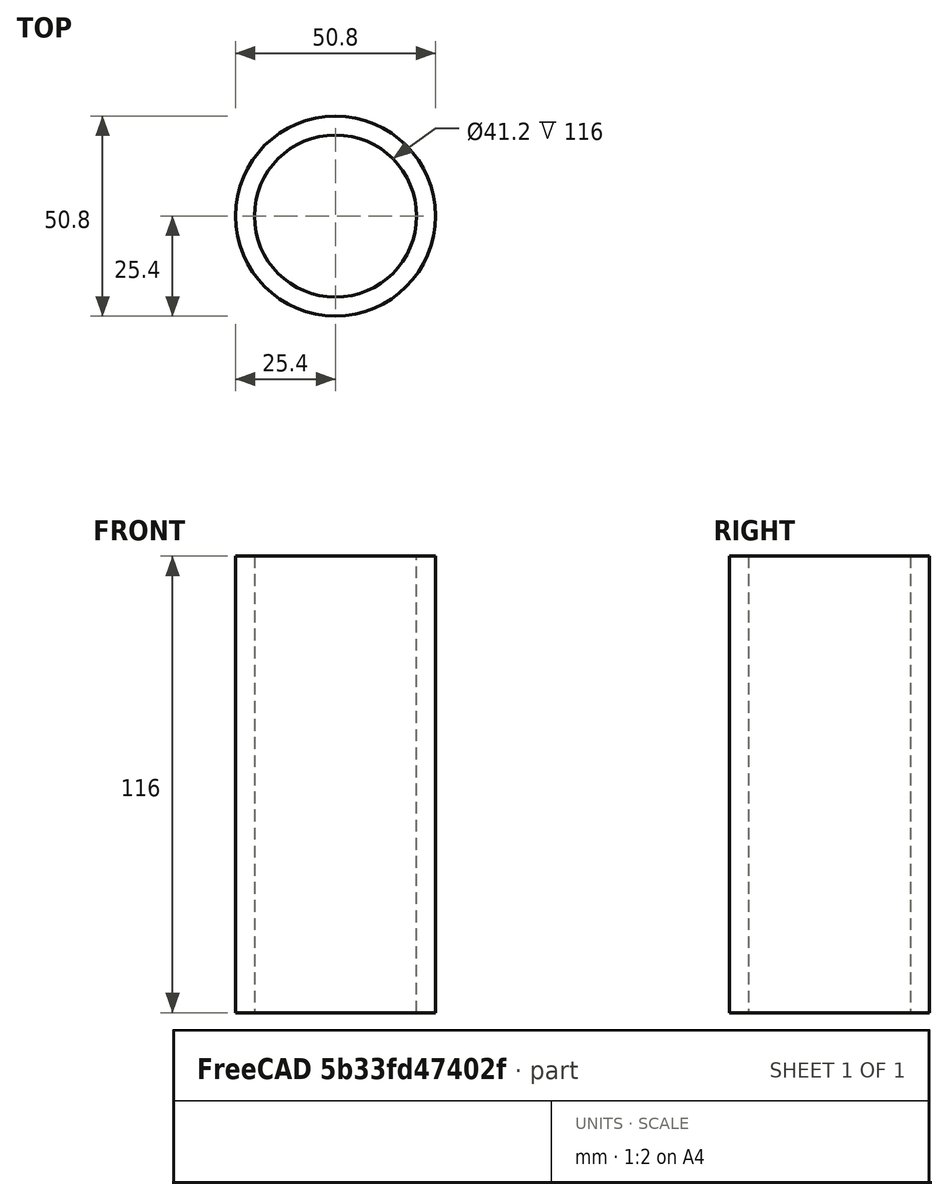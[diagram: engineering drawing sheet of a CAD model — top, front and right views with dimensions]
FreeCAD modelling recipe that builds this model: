
FCSTD DOCUMENT  (FreeCAD 0.19R24267 +99 (Git))
Label: Steel tube spacer 116mm length
License: All rights reserved
LicenseURL: http://en.wikipedia.org/wiki/All_rights_reserved
objects: Sketcher::SketchObject×1, PartDesign::Pad×1, PartDesign::Body×1
note: 4 computed .brp shape members not serialized (recipe doc carries the construction recipe); baked Part::Feature solids carry a one-line shape summary decoded from their .brp

FEATURE [Sketcher::SketchObject] Sketch  label="Cross section"
  FullyConstrained = true
  MapMode = 5
  Support = -> [XY_Plane]
  sketch-geometry (4):
    g0: Circle CenterX=0 CenterY=0 CenterZ=0 NormalX=0 NormalY=0 NormalZ=1 AngleXU=0 Radius=20.6
    g1: Circle CenterX=0 CenterY=0 CenterZ=0 NormalX=0 NormalY=0 NormalZ=1 AngleXU=0 Radius=25.4
    g2: GeomPoint X=20.6 Y=0 Z=0
    g3: GeomPoint X=25.4 Y=0 Z=0
  constraints (8):
    c: Coincident(g0,g-1)
    c: Coincident(g1,g0)
    c: PointOnObject(g2,g0)
    c: PointOnObject(g3,g1)
    c: PointOnObject(g3,g-1)
    c: PointOnObject(g2,g-1)
    c: DistanceX(g2,g3) = 4.8
    c: Diameter(g1) = 50.8
FEATURE [PartDesign::Pad] Pad  label="Length"
  Direction = (1,1,1)
  Length = 116
  Length2 = 100
  Profile = -> Sketch
  Type = 0
FEATURE [PartDesign::Body] Body
  Group = -> [Sketch,Pad]
  Origin = -> Origin
  Tip = -> Pad
